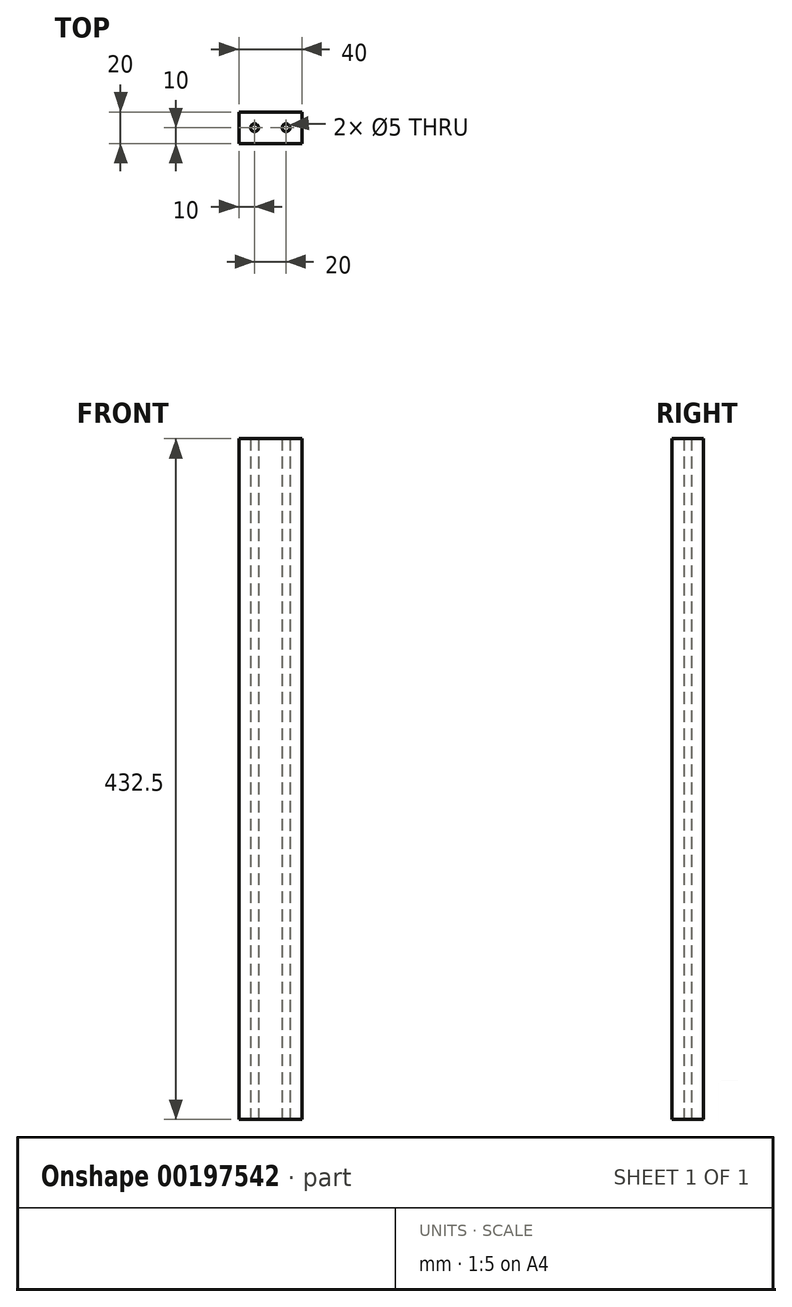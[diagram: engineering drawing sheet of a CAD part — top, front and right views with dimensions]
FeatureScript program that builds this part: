
annotation { "Feature Type Name" : "Feature", "Feature Type Description" : "" }
export const myFeature = defineFeature(function(context is Context, id is Id, definition is map)
    precondition{}
    {
        {
            var Q0;
            Q0=qCreatedBy(makeId("Top.planeOp"),FACE);
            var sketch = newSketch(context, id + "F0", { "sketchPlane" : qUnion([Q0])});
            skLineSegment(sketch, "E0.bottom", {"start": v(-20, 10) * mm, "end": v(20, 10) * mm});
            skLineSegment(sketch, "E0.top", {"start": v(-20, -10) * mm, "end": v(20, -10) * mm});
            skLineSegment(sketch, "E0.left", {"start": v(-20, 10) * mm, "end": v(-20, -10) * mm});
            skLineSegment(sketch, "E0.right", {"start": v(20, 10) * mm, "end": v(20, -10) * mm});
            skCircle(sketch, "E1", {"center": v(-10, 0) * mm, "radius": 2.5 * mm});
            skCircle(sketch, "E2", {"center": v(10, 0) * mm, "radius": 2.5 * mm});
            skSolve(sketch);
        }
        {
            var Q0;
            Q0=qSketchRegion(id+"F0",true);
            extrude(context, id + "F1", {"entities" : qUnion([Q0]), "depth" : 432.5 * mm});
        }
        {
            var Q0;
            Q0=makeQuery(id+"F1.opExtrude","SWEPT_FACE",FACE,{"disambiguationData":[OSD([sQuery(id+"F0.wireOp",EDGE,"E0.right")])]});
            var sketch = newSketch(context, id + "F2", { "sketchPlane" : qUnion([Q0])});
            skCircle(sketch, "E3", {"center": v(0, 10) * mm, "radius": 2.5 * mm});
            skSolve(sketch);
        }
        {
            var Q0;
            Q0=makeQuery(id+"F1.opExtrude","SWEPT_FACE",FACE,{"disambiguationData":[OSD([sQuery(id+"F0.wireOp",EDGE,"E0.top")])]});
            var sketch = newSketch(context, id + "F3", { "sketchPlane" : qUnion([Q0])});
            skCircle(sketch, "E4", {"center": v(0, 216.25) * mm, "radius": 2.5 * mm});
            skPoint(sketch, "E4.centerSnap0", {"position": v(-20, 216.25) * mm});
            skSolve(sketch);
        }
        {
            var Q0;
            Q0=makeQuery(id+"F3.imprint","IMPRINT",FACE,{"disambiguationData":[TD([[makeQuery(id+"F3.imprint","IMPRINT",EDGE,{"derivedFrom":sQuery(id+"F3.wireOp",EDGE,"E4")}),-1.0]])]});
            var sketch = newSketch(context, id + "F4", { "sketchPlane" : qUnion([Q0])});
            skCircle(sketch, "E5", {"center": v(10, 10) * mm, "radius": 2.5 * mm});
            skCircle(sketch, "E6", {"center": v(10, 422.5) * mm, "radius": 2.5 * mm});
            skSolve(sketch);
        }
    });
